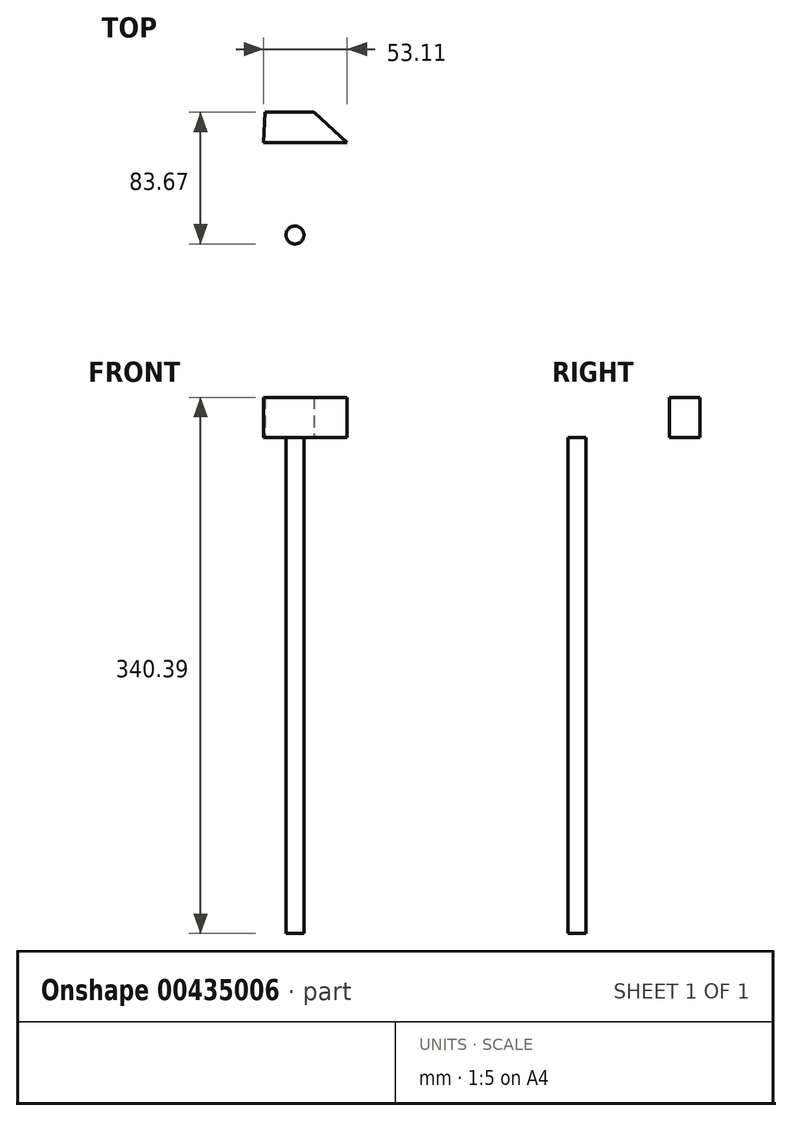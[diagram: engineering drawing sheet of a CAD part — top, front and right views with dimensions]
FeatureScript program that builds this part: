
annotation { "Feature Type Name" : "Feature", "Feature Type Description" : "" }
export const myFeature = defineFeature(function(context is Context, id is Id, definition is map)
    precondition{}
    {
        {
            var Q0;
            Q0=qCreatedBy(makeId("Top.planeOp"),FACE);
            var sketch = newSketch(context, id + "F0", { "sketchPlane" : qUnion([Q0])});
            skLineSegment(sketch, "E0", {"start": v(-19.09, 38.8) * mm, "end": v(12.24, 38.8) * mm});
            skLineSegment(sketch, "E1", {"start": v(12.24, 38.8) * mm, "end": v(33.2, 19.5) * mm});
            skLineSegment(sketch, "E2", {"start": v(33.2, 19.5) * mm, "end": v(10.79, 19.5) * mm});
            skLineSegment(sketch, "E3", {"start": v(10.79, 19.5) * mm, "end": v(-19.92, 19.5) * mm});
            skLineSegment(sketch, "E4", {"start": v(-19.92, 19.5) * mm, "end": v(-19.09, 38.8) * mm});
            skSolve(sketch);
        }
        {
            var Q0;
            Q0=makeQuery(id+"F0.imprint","IMPRINT",FACE,{"disambiguationData":[TD([[makeQuery(id+"F0.imprint","IMPRINT",EDGE,{"derivedFrom":sQuery(id+"F0.wireOp",EDGE,"E0")}),-1.0]])]});
            extrude(context, id + "F1", {"entities" : qUnion([Q0]), "depth" : 25.4 * mm});
        }
        {
            var Q0;
            Q0=qCreatedBy(makeId("Top.planeOp"),FACE);
            var sketch = newSketch(context, id + "F2", { "sketchPlane" : qUnion([Q0])});
            skCircle(sketch, "E5", {"center": v(0, -39.2) * mm, "radius": 5.67 * mm});
            skSolve(sketch);
        }
        {
            var Q0;
            Q0=makeQuery(id+"F2.imprint","IMPRINT",FACE,{"disambiguationData":[TD([[makeQuery(id+"F2.imprint","IMPRINT",EDGE,{"derivedFrom":sQuery(id+"F2.wireOp",EDGE,"E5")}),1.0]])]});
            extrude(context, id + "F3", {"entities" : qUnion([Q0]), "oppositeDirection" : true, "depth" : 315 * mm});
        }
    });
